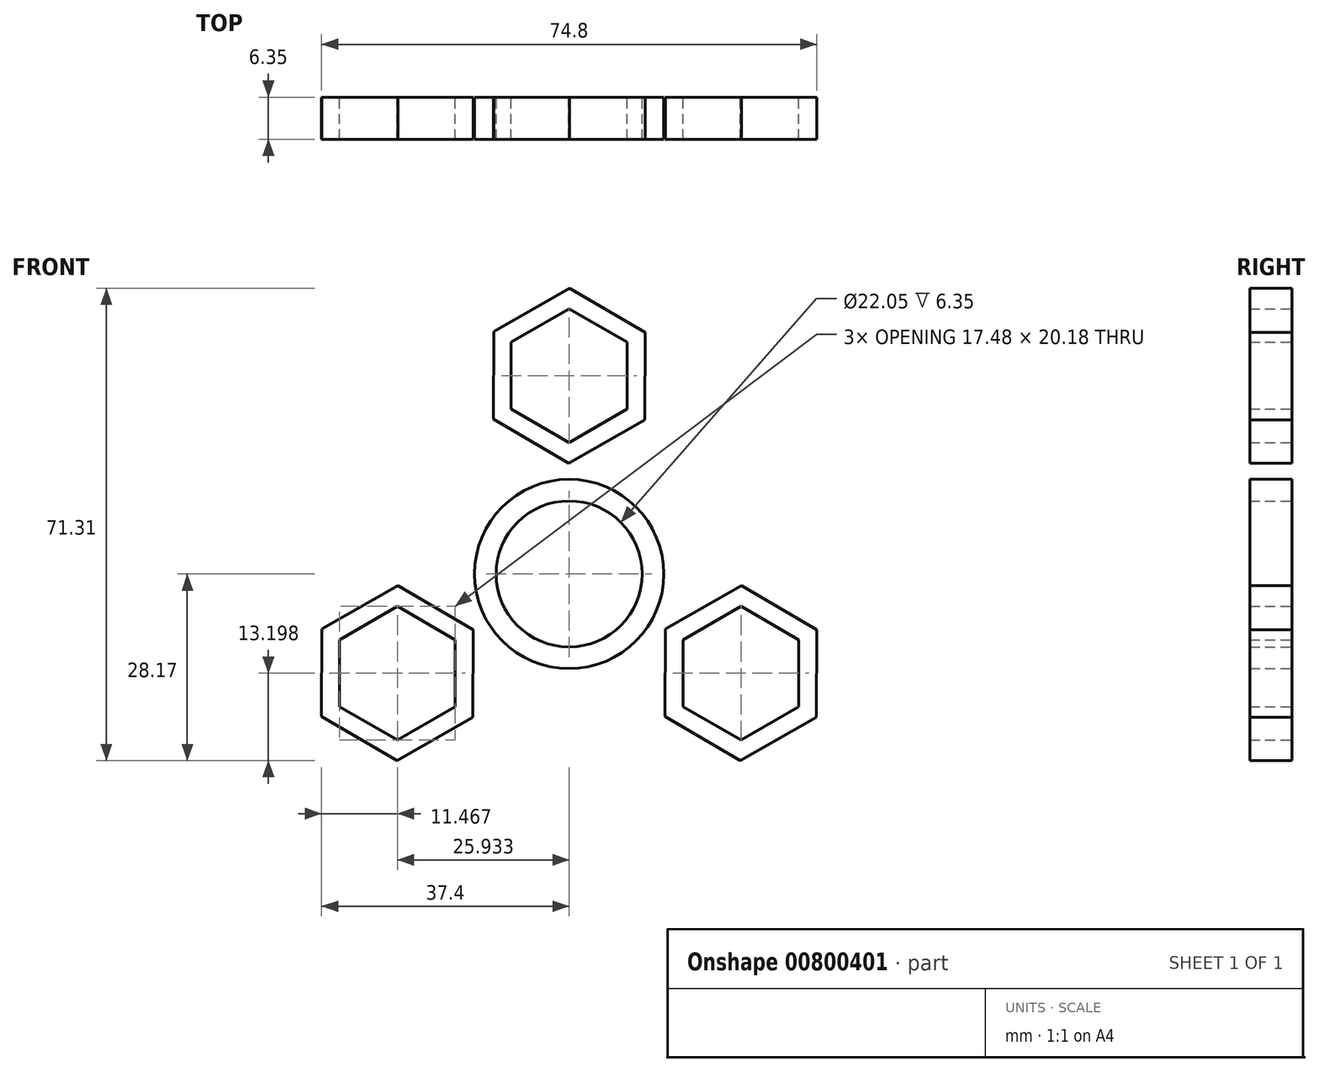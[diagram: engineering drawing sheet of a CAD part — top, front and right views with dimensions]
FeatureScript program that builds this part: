
annotation { "Feature Type Name" : "Feature", "Feature Type Description" : "" }
export const myFeature = defineFeature(function(context is Context, id is Id, definition is map)
    precondition{}
    {
        {
            var Q0;
            Q0=qCreatedBy(makeId("Front.planeOp"),FACE);
            var sketch = newSketch(context, id + "F0", { "sketchPlane" : qUnion([Q0])});
            skCircle(sketch, "E0", {"center": v(0, 0) * mm, "radius": 14.29 * mm});
            skCircle(sketch, "E1", {"center": v(0, 0) * mm, "radius": 11.02 * mm});
            skSolve(sketch);
        }
        {
            var Q0;
            Q0=qCreatedBy(makeId("Front.planeOp"),FACE);
            var sketch = newSketch(context, id + "F1", { "sketchPlane" : qUnion([Q0])});
            skCircle(sketch, "E2.cCircle", {"center": v(0, 29.94) * mm, "radius": 8.74 * mm, "construction": true});
            skLineSegment(sketch, "E2.0", {"start": v(-8.74, 24.9) * mm, "end": v(-8.74, 34.99) * mm});
            skLineSegment(sketch, "E2.1", {"start": v(-8.74, 34.99) * mm, "end": v(0, 40.03) * mm});
            skLineSegment(sketch, "E2.2", {"start": v(0, 40.03) * mm, "end": v(8.74, 34.99) * mm});
            skLineSegment(sketch, "E2.3", {"start": v(8.74, 34.99) * mm, "end": v(8.74, 24.9) * mm});
            skLineSegment(sketch, "E2.4", {"start": v(8.74, 24.9) * mm, "end": v(0, 19.86) * mm});
            skLineSegment(sketch, "E2.5", {"start": v(0, 19.86) * mm, "end": v(-8.74, 24.9) * mm});
            skPoint(sketch, "E2.0.midPoint", {"position": v(-8.74, 29.94) * mm});
            skCircle(sketch, "E3.cCircle", {"center": v(0, 29.94) * mm, "radius": 11.43 * mm, "construction": true});
            skLineSegment(sketch, "E3.0", {"start": v(-11.4, 36.6) * mm, "end": v(0.07, 43.14) * mm});
            skLineSegment(sketch, "E3.1", {"start": v(0.07, 43.14) * mm, "end": v(11.46, 36.48) * mm});
            skLineSegment(sketch, "E3.2", {"start": v(11.46, 36.48) * mm, "end": v(11.4, 23.29) * mm});
            skLineSegment(sketch, "E3.3", {"start": v(11.4, 23.29) * mm, "end": v(-0.07, 16.75) * mm});
            skLineSegment(sketch, "E3.4", {"start": v(-0.07, 16.75) * mm, "end": v(-11.46, 23.4) * mm});
            skLineSegment(sketch, "E3.5", {"start": v(-11.46, 23.4) * mm, "end": v(-11.4, 36.6) * mm});
            skPoint(sketch, "E3.0.midPoint", {"position": v(-5.66, 39.87) * mm});
            skLineSegment(sketch, "E4.1.0", {"start": v(-17.2, -9.93) * mm, "end": v(-17.2, -20.02) * mm});
            skLineSegment(sketch, "E4.1.1", {"start": v(-25.93, -4.88) * mm, "end": v(-17.2, -9.93) * mm});
            skLineSegment(sketch, "E4.1.2", {"start": v(-34.67, -20.02) * mm, "end": v(-34.67, -9.93) * mm});
            skCircle(sketch, "E4.1.3", {"center": v(-25.93, -14.97) * mm, "radius": 8.74 * mm, "construction": true});
            skCircle(sketch, "E4.1.4", {"center": v(-25.93, -14.97) * mm, "radius": 11.43 * mm, "construction": true});
            skLineSegment(sketch, "E4.1.5", {"start": v(-37.4, -21.51) * mm, "end": v(-37.33, -8.31) * mm});
            skLineSegment(sketch, "E4.1.6", {"start": v(-25.86, -1.77) * mm, "end": v(-14.47, -8.43) * mm});
            skLineSegment(sketch, "E4.1.7", {"start": v(-14.47, -8.43) * mm, "end": v(-14.54, -21.63) * mm});
            skPoint(sketch, "E4.1.8", {"position": v(-31.7, -24.84) * mm});
            skLineSegment(sketch, "E4.1.9", {"start": v(-14.54, -21.63) * mm, "end": v(-26, -28.17) * mm});
            skPoint(sketch, "E4.1.10", {"position": v(-21.56, -22.54) * mm});
            skLineSegment(sketch, "E4.1.11", {"start": v(-34.67, -9.93) * mm, "end": v(-25.93, -4.88) * mm});
            skLineSegment(sketch, "E4.1.12", {"start": v(-25.93, -25.06) * mm, "end": v(-34.67, -20.02) * mm});
            skLineSegment(sketch, "E4.1.13", {"start": v(-17.2, -20.02) * mm, "end": v(-25.93, -25.06) * mm});
            skLineSegment(sketch, "E4.1.14", {"start": v(-26, -28.17) * mm, "end": v(-37.4, -21.51) * mm});
            skLineSegment(sketch, "E4.1.15", {"start": v(-37.33, -8.31) * mm, "end": v(-25.86, -1.77) * mm});
            skLineSegment(sketch, "E4.2.0", {"start": v(17.2, -9.93) * mm, "end": v(25.93, -4.88) * mm});
            skLineSegment(sketch, "E4.2.1", {"start": v(17.2, -20.02) * mm, "end": v(17.2, -9.93) * mm});
            skLineSegment(sketch, "E4.2.2", {"start": v(34.67, -20.02) * mm, "end": v(25.93, -25.06) * mm});
            skCircle(sketch, "E4.2.3", {"center": v(25.93, -14.97) * mm, "radius": 8.74 * mm, "construction": true});
            skCircle(sketch, "E4.2.4", {"center": v(25.93, -14.97) * mm, "radius": 11.43 * mm, "construction": true});
            skLineSegment(sketch, "E4.2.5", {"start": v(37.33, -21.63) * mm, "end": v(25.86, -28.17) * mm});
            skLineSegment(sketch, "E4.2.6", {"start": v(14.47, -21.51) * mm, "end": v(14.54, -8.31) * mm});
            skLineSegment(sketch, "E4.2.7", {"start": v(14.54, -8.31) * mm, "end": v(26, -1.77) * mm});
            skPoint(sketch, "E4.2.8", {"position": v(37.36, -15.03) * mm});
            skLineSegment(sketch, "E4.2.9", {"start": v(26, -1.77) * mm, "end": v(37.4, -8.43) * mm});
            skPoint(sketch, "E4.2.10", {"position": v(30.3, -7.4) * mm});
            skLineSegment(sketch, "E4.2.11", {"start": v(25.93, -25.06) * mm, "end": v(17.2, -20.02) * mm});
            skLineSegment(sketch, "E4.2.12", {"start": v(34.67, -9.93) * mm, "end": v(34.67, -20.02) * mm});
            skLineSegment(sketch, "E4.2.13", {"start": v(25.93, -4.88) * mm, "end": v(34.67, -9.93) * mm});
            skLineSegment(sketch, "E4.2.14", {"start": v(37.4, -8.43) * mm, "end": v(37.33, -21.63) * mm});
            skLineSegment(sketch, "E4.2.15", {"start": v(25.86, -28.17) * mm, "end": v(14.47, -21.51) * mm});
            skPoint(sketch, "E4.center", {"position": v(0, 0) * mm});
            skSolve(sketch);
        }
        {
            var Q0;
            Q0=makeQuery(id+"F1.imprint","IMPRINT",FACE,{"disambiguationData":[TD([[makeQuery(id+"F1.imprint","IMPRINT",EDGE,{"derivedFrom":sQuery(id+"F1.wireOp",EDGE,"E2.0")}),1.0]])]});
            var Q1;
            Q1=makeQuery(id+"F1.imprint","IMPRINT",FACE,{"disambiguationData":[TD([[makeQuery(id+"F1.imprint","IMPRINT",EDGE,{"derivedFrom":sQuery(id+"F1.wireOp",EDGE,"E4.2.0")}),1.0]])]});
            var Q2;
            Q2=makeQuery(id+"F0.imprint","IMPRINT",FACE,{"disambiguationData":[TD([[makeQuery(id+"F0.imprint","IMPRINT",EDGE,{"derivedFrom":sQuery(id+"F0.wireOp",EDGE,"E0")}),1.0]])]});
            var Q3;
            Q3=makeQuery(id+"F1.imprint","IMPRINT",FACE,{"disambiguationData":[TD([[makeQuery(id+"F1.imprint","IMPRINT",EDGE,{"derivedFrom":sQuery(id+"F1.wireOp",EDGE,"E4.1.0")}),1.0]])]});
            extrude(context, id + "F2", {"entities" : qUnion([Q0, Q1, Q2, Q3]), "depth" : 6.35 * mm, "offsetDistance" : 25.4 * mm});
        }
    });
